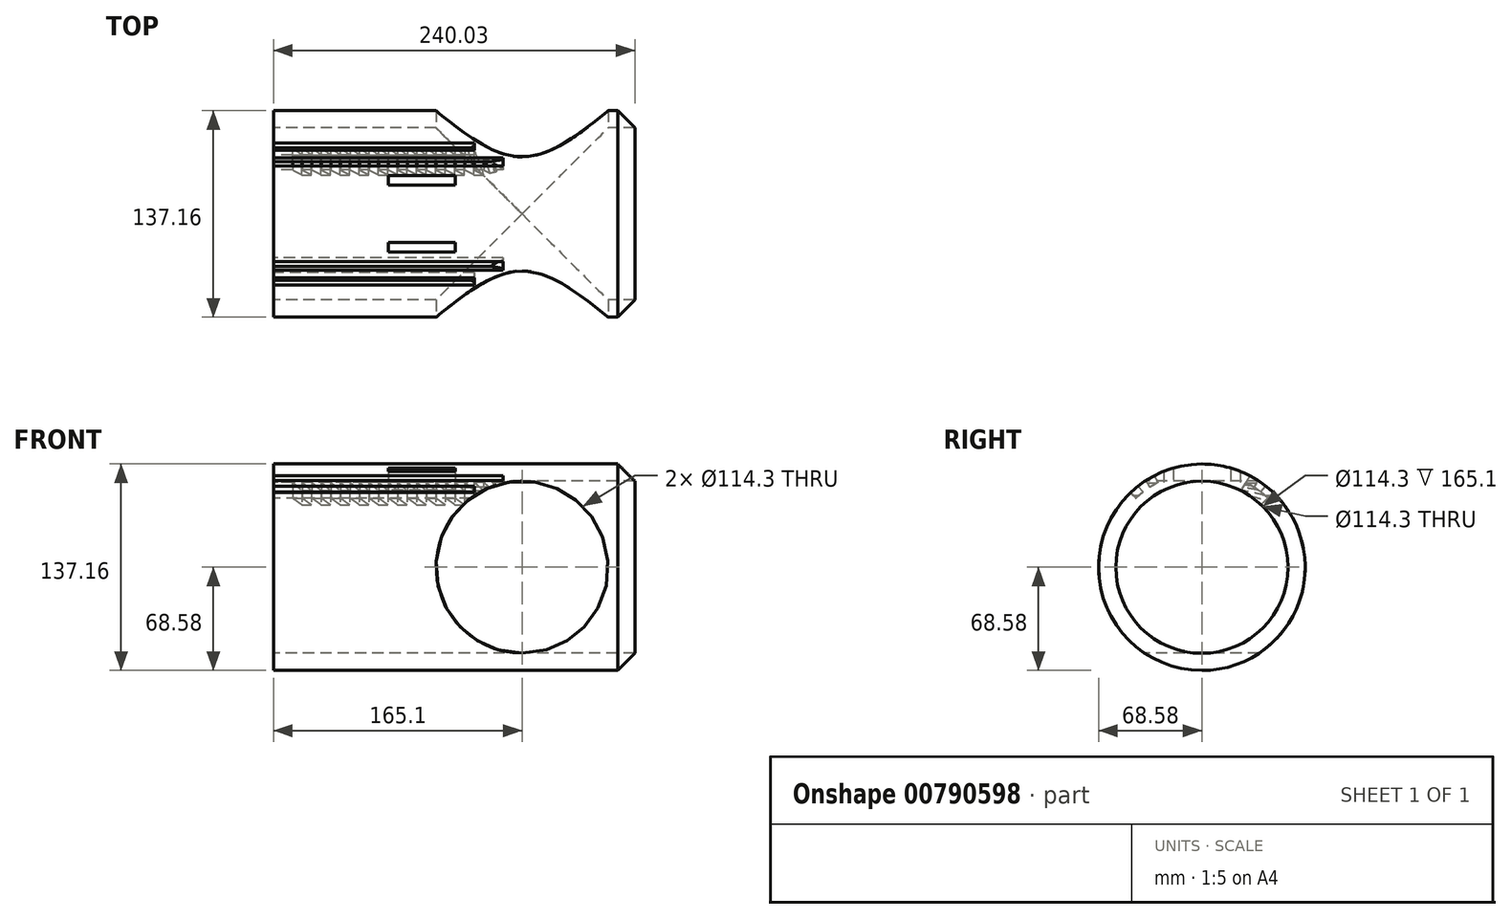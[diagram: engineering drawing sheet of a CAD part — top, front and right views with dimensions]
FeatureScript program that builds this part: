
annotation { "Feature Type Name" : "Feature", "Feature Type Description" : "" }
export const myFeature = defineFeature(function(context is Context, id is Id, definition is map)
    precondition{}
    {
        {
            var Q0;
            Q0=qCreatedBy(makeId("Right.planeOp"),FACE);
            var sketch = newSketch(context, id + "F0", { "sketchPlane" : qUnion([Q0])});
            skCircle(sketch, "E0", {"center": v(0, 0) * mm, "radius": 57.15 * mm});
            skCircle(sketch, "E1", {"center": v(0, 0) * mm, "radius": 68.58 * mm});
            skLineSegment(sketch, "E2", {"start": v(31.75, 60.79) * mm, "end": v(29.2, 56.4) * mm});
            skLineSegment(sketch, "E3", {"start": v(29.2, 56.4) * mm, "end": v(34.68, 53.2) * mm});
            skLineSegment(sketch, "E4", {"start": v(34.68, 53.2) * mm, "end": v(37.24, 57.6) * mm});
            skLineSegment(sketch, "E5", {"start": v(-31.75, 60.79) * mm, "end": v(-29.2, 56.4) * mm});
            skLineSegment(sketch, "E6", {"start": v(-29.2, 56.4) * mm, "end": v(-34.68, 53.2) * mm});
            skLineSegment(sketch, "E7", {"start": v(-34.68, 53.2) * mm, "end": v(-37.24, 57.6) * mm});
            skLineSegment(sketch, "E8", {"start": v(-42.4, 53.9) * mm, "end": v(-39.08, 50.06) * mm});
            skLineSegment(sketch, "E9", {"start": v(-39.08, 50.06) * mm, "end": v(-43.88, 45.9) * mm});
            skLineSegment(sketch, "E10", {"start": v(-43.88, 45.9) * mm, "end": v(-47.2, 49.75) * mm});
            skLineSegment(sketch, "E11", {"start": v(47.2, 49.75) * mm, "end": v(43.88, 45.9) * mm});
            skLineSegment(sketch, "E12", {"start": v(43.88, 45.9) * mm, "end": v(39.08, 50.06) * mm});
            skLineSegment(sketch, "E13", {"start": v(39.08, 50.06) * mm, "end": v(42.4, 53.9) * mm});
            skSolve(sketch);
        }
        {
            var Q0;
            Q0=makeQuery(id+"F0.imprint","IMPRINT",FACE,{"disambiguationData":[TD([[makeQuery(id+"F0.imprint","IMPRINT",EDGE,{"derivedFrom":sQuery(id+"F0.wireOp",EDGE,"E0")}),-1.0]])]});
            var Q1;
            {var subQ0=sQuery(id+"F0.wireOp",EDGE,"E8");Q1=makeQuery(id+"F0.imprint","IMPRINT",FACE,{"disambiguationData":[TD([[makeQuery(id+"F0.imprint","IMPRINT",EDGE,{"derivedFrom":subQ0}),-1.0]])]});}
            var Q2;
            {var subQ0=sQuery(id+"F0.wireOp",EDGE,"E5");Q2=makeQuery(id+"F0.imprint","IMPRINT",FACE,{"disambiguationData":[TD([[makeQuery(id+"F0.imprint","IMPRINT",EDGE,{"derivedFrom":subQ0}),-1.0]])]});}
            var Q3;
            {var subQ0=sQuery(id+"F0.wireOp",EDGE,"E2");Q3=makeQuery(id+"F0.imprint","IMPRINT",FACE,{"disambiguationData":[TD([[makeQuery(id+"F0.imprint","IMPRINT",EDGE,{"derivedFrom":subQ0}),1.0]])]});}
            var Q4;
            {var subQ0=sQuery(id+"F0.wireOp",EDGE,"E11");Q4=makeQuery(id+"F0.imprint","IMPRINT",FACE,{"disambiguationData":[TD([[makeQuery(id+"F0.imprint","IMPRINT",EDGE,{"derivedFrom":subQ0}),-1.0]])]});}
            extrude(context, id + "F1", {"entities" : qUnion([Q0, Q1, Q2, Q3, Q4]), "depth" : 241.3 * mm, "offsetDistance" : 25.4 * mm});
        }
        {
            var Q0;
            Q0=qCreatedBy(makeId("Front.planeOp"),FACE);
            var sketch = newSketch(context, id + "F2", { "sketchPlane" : qUnion([Q0])});
            skLineSegment(sketch, "E14", {"start": v(0, 0) * mm, "end": v(165.1, 0) * mm});
            skCircle(sketch, "E15", {"center": v(165.1, 0) * mm, "radius": 57.15 * mm});
            skSolve(sketch);
        }
        {
            var Q0;
            {var subQ0=sQuery(id+"F0.wireOp",EDGE,"E8");Q0=makeQuery(id+"F0.imprint","IMPRINT",FACE,{"disambiguationData":[TD([[makeQuery(id+"F0.imprint","IMPRINT",EDGE,{"derivedFrom":subQ0}),-1.0]])]});}
            var Q1;
            {var subQ0=sQuery(id+"F0.wireOp",EDGE,"E11");Q1=makeQuery(id+"F0.imprint","IMPRINT",FACE,{"disambiguationData":[TD([[makeQuery(id+"F0.imprint","IMPRINT",EDGE,{"derivedFrom":subQ0}),-1.0]])]});}
            extrude(context, id + "F3", {"entities" : qUnion([Q0, Q1]), "operationType" : NewBodyOperationType.REMOVE, "depth" : 133.35 * mm, "offsetDistance" : 25.4 * mm});
        }
        {
            var Q0;
            {var subQ0=sQuery(id+"F0.wireOp",EDGE,"E5");Q0=makeQuery(id+"F0.imprint","IMPRINT",FACE,{"disambiguationData":[TD([[makeQuery(id+"F0.imprint","IMPRINT",EDGE,{"derivedFrom":subQ0}),-1.0]])]});}
            var Q1;
            {var subQ0=sQuery(id+"F0.wireOp",EDGE,"E2");Q1=makeQuery(id+"F0.imprint","IMPRINT",FACE,{"disambiguationData":[TD([[makeQuery(id+"F0.imprint","IMPRINT",EDGE,{"derivedFrom":subQ0}),1.0]])]});}
            extrude(context, id + "F4", {"entities" : qUnion([Q0, Q1]), "operationType" : NewBodyOperationType.REMOVE, "depth" : 152.4 * mm, "offsetDistance" : 25.4 * mm});
        }
        {
            var Q0;
            Q0=makeQuery(id+"F2.imprint","IMPRINT",FACE,{"disambiguationData":[TD([[makeQuery(id+"F2.imprint","IMPRINT",EDGE,{"derivedFrom":sQuery(id+"F2.wireOp",EDGE,"E15")}),1.0]])]});
            extrude(context, id + "F5", {"entities" : qUnion([Q0]), "operationType" : NewBodyOperationType.REMOVE, "endBound" : BoundingType.SYMMETRIC, "oppositeDirection" : true, "depth" : 152.4 * mm, "offsetDistance" : 25.4 * mm});
        }
        {
            var Q0;
            Q0=makeQuery(id+"F1.opExtrude","CAP_EDGE",EDGE,{"disambiguationData":[OSD([sQuery(id+"F0.wireOp",EDGE,"E1")])],"isStart":false});
            chamfer(context, id + "F6", {"entities" : qUnion([Q0]), "chamferType" : ChamferType.TWO_OFFSETS, "width1" : 12.7 * mm, "oppositeDirection" : false, "width2" : 12.7 * mm, "tangentPropagation" : true});
        }
        {
            var Q0;
            Q0=makeQuery(id+"F4.boolean.opBoolean","COPY",FACE,{"derivedFrom":makeQuery(id+"F4.opExtrude","SWEPT_FACE",FACE,{"disambiguationData":[OSD([sQuery(id+"F0.wireOp",EDGE,"E3")])]})});
            var sketch = newSketch(context, id + "F7", { "sketchPlane" : qUnion([Q0])});
            skLineSegment(sketch, "E16.bottom", {"start": v(31.75, -3.18) * mm, "end": v(25.4, -3.18) * mm});
            skLineSegment(sketch, "E16.top", {"start": v(31.75, 3.17) * mm, "end": v(25.4, 3.17) * mm});
            skLineSegment(sketch, "E16.left", {"start": v(31.75, -3.18) * mm, "end": v(31.75, 3.17) * mm});
            skLineSegment(sketch, "E16.right", {"start": v(25.4, -3.18) * mm, "end": v(25.4, 3.17) * mm});
            skLineSegment(sketch, "E17.bottom", {"start": v(19.05, -3.18) * mm, "end": v(12.7, -3.18) * mm});
            skLineSegment(sketch, "E17.top", {"start": v(19.05, 3.17) * mm, "end": v(12.7, 3.17) * mm});
            skLineSegment(sketch, "E17.left", {"start": v(19.05, -3.18) * mm, "end": v(19.05, 3.17) * mm});
            skLineSegment(sketch, "E17.right", {"start": v(12.7, -3.18) * mm, "end": v(12.7, 3.17) * mm});
            skLineSegment(sketch, "E18.bottom", {"start": v(57.15, -3.18) * mm, "end": v(50.8, -3.18) * mm});
            skLineSegment(sketch, "E18.top", {"start": v(57.15, 3.17) * mm, "end": v(50.8, 3.17) * mm});
            skLineSegment(sketch, "E18.left", {"start": v(57.15, -3.18) * mm, "end": v(57.15, 3.17) * mm});
            skLineSegment(sketch, "E18.right", {"start": v(50.8, -3.18) * mm, "end": v(50.8, 3.17) * mm});
            skLineSegment(sketch, "E19.bottom", {"start": v(44.45, -3.18) * mm, "end": v(38.1, -3.18) * mm});
            skLineSegment(sketch, "E19.top", {"start": v(44.45, 3.17) * mm, "end": v(38.1, 3.17) * mm});
            skLineSegment(sketch, "E19.left", {"start": v(44.45, -3.18) * mm, "end": v(44.45, 3.17) * mm});
            skLineSegment(sketch, "E19.right", {"start": v(38.1, -3.18) * mm, "end": v(38.1, 3.17) * mm});
            skLineSegment(sketch, "E20.bottom", {"start": v(82.55, -3.18) * mm, "end": v(76.2, -3.18) * mm});
            skLineSegment(sketch, "E20.top", {"start": v(82.55, 3.17) * mm, "end": v(76.2, 3.17) * mm});
            skLineSegment(sketch, "E20.left", {"start": v(82.55, -3.18) * mm, "end": v(82.55, 3.17) * mm});
            skLineSegment(sketch, "E20.right", {"start": v(76.2, -3.18) * mm, "end": v(76.2, 3.17) * mm});
            skLineSegment(sketch, "E21.bottom", {"start": v(69.85, -3.18) * mm, "end": v(63.5, -3.18) * mm});
            skLineSegment(sketch, "E21.top", {"start": v(69.85, 3.17) * mm, "end": v(63.5, 3.17) * mm});
            skLineSegment(sketch, "E21.left", {"start": v(69.85, -3.18) * mm, "end": v(69.85, 3.17) * mm});
            skLineSegment(sketch, "E21.right", {"start": v(63.5, -3.18) * mm, "end": v(63.5, 3.17) * mm});
            skLineSegment(sketch, "E22.bottom", {"start": v(107.95, -3.18) * mm, "end": v(101.6, -3.18) * mm});
            skLineSegment(sketch, "E22.top", {"start": v(107.95, 3.17) * mm, "end": v(101.6, 3.17) * mm});
            skLineSegment(sketch, "E22.left", {"start": v(107.95, -3.18) * mm, "end": v(107.95, 3.17) * mm});
            skLineSegment(sketch, "E22.right", {"start": v(101.6, -3.18) * mm, "end": v(101.6, 3.17) * mm});
            skLineSegment(sketch, "E23.bottom", {"start": v(95.25, -3.18) * mm, "end": v(88.9, -3.18) * mm});
            skLineSegment(sketch, "E23.top", {"start": v(95.25, 3.17) * mm, "end": v(88.9, 3.17) * mm});
            skLineSegment(sketch, "E23.left", {"start": v(95.25, -3.18) * mm, "end": v(95.25, 3.17) * mm});
            skLineSegment(sketch, "E23.right", {"start": v(88.9, -3.18) * mm, "end": v(88.9, 3.17) * mm});
            skLineSegment(sketch, "E24.bottom", {"start": v(120.65, -3.18) * mm, "end": v(114.3, -3.18) * mm});
            skLineSegment(sketch, "E24.top", {"start": v(120.65, 3.17) * mm, "end": v(114.3, 3.17) * mm});
            skLineSegment(sketch, "E24.left", {"start": v(120.65, -3.18) * mm, "end": v(120.65, 3.17) * mm});
            skLineSegment(sketch, "E24.right", {"start": v(114.3, -3.18) * mm, "end": v(114.3, 3.17) * mm});
            skLineSegment(sketch, "E25.bottom", {"start": v(146.05, -3.18) * mm, "end": v(139.7, -3.18) * mm});
            skLineSegment(sketch, "E25.top", {"start": v(146.05, 3.17) * mm, "end": v(139.7, 3.17) * mm});
            skLineSegment(sketch, "E25.left", {"start": v(146.05, -3.18) * mm, "end": v(146.05, 3.17) * mm});
            skLineSegment(sketch, "E25.right", {"start": v(139.7, -3.18) * mm, "end": v(139.7, 3.17) * mm});
            skLineSegment(sketch, "E26.bottom", {"start": v(133.35, -3.18) * mm, "end": v(127, -3.18) * mm});
            skLineSegment(sketch, "E26.top", {"start": v(133.35, 3.17) * mm, "end": v(127, 3.17) * mm});
            skLineSegment(sketch, "E26.left", {"start": v(133.35, -3.18) * mm, "end": v(133.35, 3.17) * mm});
            skLineSegment(sketch, "E26.right", {"start": v(127, -3.18) * mm, "end": v(127, 3.17) * mm});
            skSolve(sketch);
        }
        {
            var Q0;
            Q0=makeQuery(id+"F0.imprint","IMPRINT",FACE,{"disambiguationData":[TD([[makeQuery(id+"F0.imprint","IMPRINT",EDGE,{"derivedFrom":sQuery(id+"F0.wireOp",EDGE,"E0")}),-1.0]])]});
            var sketch = newSketch(context, id + "F8", { "sketchPlane" : qUnion([Q0])});
            skLineSegment(sketch, "E27", {"start": v(29.2, 56.4) * mm, "end": v(25.99, 50.9) * mm});
            skLineSegment(sketch, "E28", {"start": v(39.08, 50.06) * mm, "end": v(34.92, 45.24) * mm});
            skSolve(sketch);
        }
        {
            var Q0;
            Q0=makeQuery(id+"F4.boolean.opBoolean","COPY",FACE,{"derivedFrom":makeQuery(id+"F4.opExtrude","SWEPT_FACE",FACE,{"disambiguationData":[OSD([sQuery(id+"F0.wireOp",EDGE,"E2")])]})});
            var sketch = newSketch(context, id + "F9", { "sketchPlane" : qUnion([Q0])});
            skLineSegment(sketch, "E29", {"start": v(0, 57.06) * mm, "end": v(-152.4, 57.06) * mm});
            skLineSegment(sketch, "E30", {"start": v(-12.7, 63.43) * mm, "end": v(-18.9, 57.06) * mm});
            skLineSegment(sketch, "E31", {"start": v(-19.05, 63.43) * mm, "end": v(-25.25, 57.06) * mm});
            skLineSegment(sketch, "E32", {"start": v(-12.7, 63.43) * mm, "end": v(-19.05, 63.43) * mm});
            skLineSegment(sketch, "E33", {"start": v(-31.6, 57.06) * mm, "end": v(-25.4, 63.43) * mm});
            skLineSegment(sketch, "E34", {"start": v(-25.4, 63.43) * mm, "end": v(-31.75, 63.43) * mm});
            skLineSegment(sketch, "E35", {"start": v(-31.75, 63.43) * mm, "end": v(-37.95, 57.06) * mm});
            skLineSegment(sketch, "E36", {"start": v(-38.1, 63.43) * mm, "end": v(-44.3, 57.06) * mm});
            skLineSegment(sketch, "E37", {"start": v(-44.45, 63.43) * mm, "end": v(-50.65, 57.06) * mm});
            skLineSegment(sketch, "E38", {"start": v(-38.1, 63.43) * mm, "end": v(-44.45, 63.43) * mm});
            skLineSegment(sketch, "E39", {"start": v(-57, 57.06) * mm, "end": v(-50.8, 63.43) * mm});
            skLineSegment(sketch, "E40", {"start": v(-50.8, 63.43) * mm, "end": v(-57.15, 63.43) * mm});
            skLineSegment(sketch, "E41", {"start": v(-57.15, 63.43) * mm, "end": v(-63.35, 57.06) * mm});
            skLineSegment(sketch, "E42", {"start": v(-101.6, 63.43) * mm, "end": v(-107.8, 57.06) * mm});
            skLineSegment(sketch, "E43", {"start": v(-107.95, 63.43) * mm, "end": v(-114.15, 57.06) * mm});
            skLineSegment(sketch, "E44", {"start": v(-101.6, 63.43) * mm, "end": v(-107.95, 63.43) * mm});
            skLineSegment(sketch, "E45", {"start": v(-95.1, 57.06) * mm, "end": v(-88.9, 63.43) * mm});
            skLineSegment(sketch, "E46", {"start": v(-88.9, 63.43) * mm, "end": v(-95.25, 63.43) * mm});
            skLineSegment(sketch, "E47", {"start": v(-95.25, 63.43) * mm, "end": v(-101.45, 57.06) * mm});
            skLineSegment(sketch, "E48", {"start": v(-63.5, 63.43) * mm, "end": v(-69.7, 57.06) * mm});
            skLineSegment(sketch, "E49", {"start": v(-69.85, 63.43) * mm, "end": v(-76.05, 57.06) * mm});
            skLineSegment(sketch, "E50", {"start": v(-63.5, 63.43) * mm, "end": v(-69.85, 63.43) * mm});
            skLineSegment(sketch, "E51", {"start": v(-82.4, 57.06) * mm, "end": v(-76.2, 63.43) * mm});
            skLineSegment(sketch, "E52", {"start": v(-76.2, 63.43) * mm, "end": v(-82.55, 63.43) * mm});
            skLineSegment(sketch, "E53", {"start": v(-82.55, 63.43) * mm, "end": v(-88.75, 57.06) * mm});
            skLineSegment(sketch, "E54", {"start": v(-139.7, 63.43) * mm, "end": v(-145.9, 57.06) * mm});
            skLineSegment(sketch, "E55", {"start": v(-146.05, 63.43) * mm, "end": v(-152.25, 57.06) * mm});
            skLineSegment(sketch, "E56", {"start": v(-139.7, 63.43) * mm, "end": v(-146.05, 63.43) * mm});
            skLineSegment(sketch, "E57", {"start": v(-133.2, 57.06) * mm, "end": v(-127, 63.43) * mm});
            skLineSegment(sketch, "E58", {"start": v(-127, 63.43) * mm, "end": v(-133.35, 63.43) * mm});
            skLineSegment(sketch, "E59", {"start": v(-133.35, 63.43) * mm, "end": v(-139.55, 57.06) * mm});
            skLineSegment(sketch, "E60", {"start": v(-120.5, 57.06) * mm, "end": v(-114.3, 63.43) * mm});
            skLineSegment(sketch, "E61", {"start": v(-114.3, 63.43) * mm, "end": v(-120.65, 63.43) * mm});
            skLineSegment(sketch, "E62", {"start": v(-120.65, 63.43) * mm, "end": v(-126.85, 57.06) * mm});
            skLineSegment(sketch, "E63", {"start": v(-152.4, 63.43) * mm, "end": v(-152.4, 57.06) * mm});
            skSolve(sketch);
        }
        {
            var Q0;
            Q0 = qSketchRegion(id + "F9", true);
            var Q1;
            Q1=sQuery(id+"F2.wireOp",EDGE,"E14");
            revolve(context, id + "F10", {"operationType" : NewBodyOperationType.REMOVE, "surfaceOperationType" : NewSurfaceOperationType.NEW, "entities" : qUnion([Q0]), "axis" : qUnion([Q1]), "revolveType" : RevolveType.ONE_DIRECTION, "oppositeDirection" : true, "angle" : 16.3 * degree});
        }
        {
            var Q0;
            Q0=qCreatedBy(makeId("Top.planeOp"),FACE);
            var sketch = newSketch(context, id + "F11", { "sketchPlane" : qUnion([Q0])});
            skLineSegment(sketch, "E64.bottom", {"start": v(120.65, -25.4) * mm, "end": v(76.2, -25.4) * mm});
            skLineSegment(sketch, "E64.top", {"start": v(120.65, -19.05) * mm, "end": v(76.2, -19.05) * mm});
            skLineSegment(sketch, "E64.left", {"start": v(120.65, -25.4) * mm, "end": v(120.65, -19.05) * mm});
            skLineSegment(sketch, "E64.right", {"start": v(76.2, -25.4) * mm, "end": v(76.2, -19.05) * mm});
            skLineSegment(sketch, "E65.bottom", {"start": v(76.2, 25.4) * mm, "end": v(120.65, 25.4) * mm});
            skLineSegment(sketch, "E65.top", {"start": v(76.2, 19.05) * mm, "end": v(120.65, 19.05) * mm});
            skLineSegment(sketch, "E65.left", {"start": v(76.2, 25.4) * mm, "end": v(76.2, 19.05) * mm});
            skLineSegment(sketch, "E65.right", {"start": v(120.65, 25.4) * mm, "end": v(120.65, 19.05) * mm});
            skSolve(sketch);
        }
        {
            var Q0;
            Q0 = qSketchRegion(id + "F11", true);
            extrude(context, id + "F12", {"entities" : qUnion([Q0]), "operationType" : NewBodyOperationType.REMOVE, "depth" : 381 * mm, "offsetDistance" : 25.4 * mm});
        }
    });
